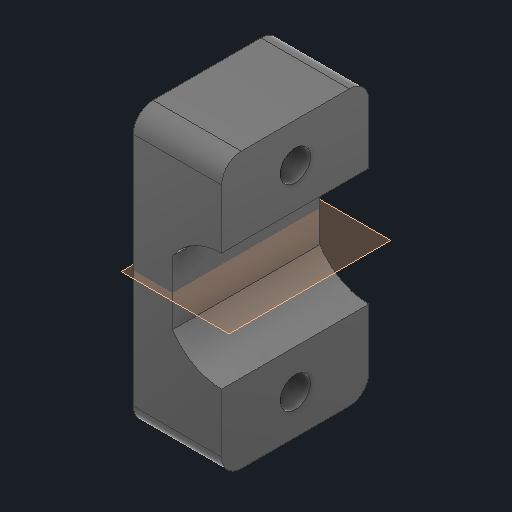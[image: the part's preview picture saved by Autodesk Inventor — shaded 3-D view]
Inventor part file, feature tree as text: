
AUTODESK INVENTOR PART (.ipt)
format: ipt  version: 2024 (Build 280153000, 153)  size: 155,136 bytes
history: native  units: in
note: dims shown in document units (in); Inventor stores cm internally (conversion verified against a paired STEP export)
features: sketch x2, extrude x1, plane x1, hole x1, fillet x1
ambient origin geometry x8: Origin, YZ Plane, XZ Plane, XY Plane, X Axis, Y Axis, Z Axis, Center Point
bodies: Body1 (feature_tree)
feature tree (6):
  extrude  "Extrusion2"  Depth=0.3543in
  plane  "Work Plane1"
  hole  "Hole1"  [1 undecoded]
  fillet  "Fillet1"  Radius=0.1575in
  sketch  "Sketch2"  dims[d8=0.5906in d9=0.0in d10=0.3543in]
  sketch  "Sketch3"  dims[d11=0.1575in d16=0.2953in d17=0.1575in d18=0.1575in d19=0.2953in d20=0.122in d21=0.2362in d22=0.1575in d23=0.0787in d24=90.0deg d25=0.315in d26=0.8108in d27=0.0787in]
note: 1 required parameter value undecoded (feature->parameter linkage not recoverable at this tier; creation-order binding heuristic only, values carry confidence <= 0.55)
